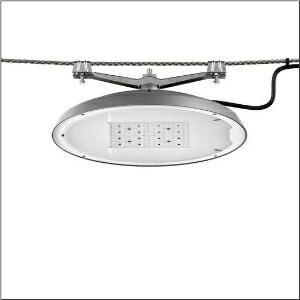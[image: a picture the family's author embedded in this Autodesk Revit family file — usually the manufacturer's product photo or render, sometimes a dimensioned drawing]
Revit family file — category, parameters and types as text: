
# Revit family: dl_50_iq_mini___st1_0s_5xa248w21f08le_fd6c
name_source: partatom
category: Lighting Fixtures
units: mm (PartAtom-declared; Revit-internal decimal feet)

## family parameters
Cut with Voids When Loaded = No
Host = Face
Light Source = No
Part Type = Normal
Room Calculation Point = No
Round Connector Dimension = Use Diameter
Shared = No

## types (1)
- --- (1 x LED, 8560 lm, 66.9 W, 2200K)
    Apparent Load = 67 VA
    CIE Flux Codes = 37 72 97 100 100
    Color Rendering = 70
    Color Temperature = 2200K
    Default Elevation = 1800 mm
    Description = DL 50 iQ mini, catenary luminaire, primary light control with lens, of PMMA, primary optical cover: cover, of toughened safety glass, transparent, light distribution: ST1.0s, light emission: direct distribution, primary light characteristic: symmetric, installation type: suspended mounting, LED, High Power LED, rated luminous flux: 8.560lm, luminous efficacy: 128lm/W, light colour: 722, colour temperature: 2200K, control gear: iQ Street-Remote, control: optimised constant luminous flux control (CLO 2.0), Desk-Remote (wireless, voltage-free reading and setting of iQ features in the workshop via application-optimized NFC function/RFID function), Light-Fading, Smart-Wire, Night-Set, Lumen-Switch, Temp-Guard, Auto-Match, Street-Remote, mains connection: 230..240V, AC, 50/60Hz, start of lifetime: 67W, end of service life: 70W, reduction: 31W, luminaire housing, of diecast aluminium, powder-coated, SITECO metallic grey (DB 702S), diameter: 500mm, height: 115mm, mounting height: 4..12m, protection rating (complete): IP66, insulation class (complete): insulation class II (safety insulation), certification: CE, ENEC, ENEC+, VDE, impact resistance: IK08, permissible operating ambient temperature for outdoor applications: -25..+40°C, standard-compliant lighting for roads and squares, packaging unit: 1 piece

Light Distribution: ST1.0s
    Height = 124 mm  [stored 0.406824 ft]
    Lamp = 1 x LED
    Lamp Light Flux = 8560 lm
    Lamp Power = 66.9 W
    Lamp count = 1
    Length = 500 mm
    Luminous efficacy = 128 lm/W
    Manufacturer = Siteco
    ModVariant = No
    Model = 5XA248W21F08LE
    Number of Poles = 1
    OnlyDefault = Yes
    Power Factor = 1
    Product Name = DL 50 iQ mini | ST1.0s
    Product group = catenary luminaire
    ProductGroupID = 6300
    Protection Class = Protection class II
    Protection Degree = IP 66
    RLX_Detail_Level = 1
    RLX_Emergency_Light_Flux = 0 lm
    RLX_Emergency_Type = 0
    RLX_Emergency_Type_DB = No
    RlxData = <blob elided: 127069 chars, md5=93f7c056>
    Socket = socket
    Standby Power = 0 W
    System Light Flux = 8560 lm
    System Power = 67 W
    Type Comments = factory setting: luminous flux: 100 % | dim-lin: 254 | 700 mA
    Type Image = l_1251783.jpg
    URL = http://relux.com
    VarID = @adj_140059
    Voltage = 0 V
    Weight = 0.00 kg
    Width = 0 mm  [stored 0 ft]

note: [stored X ft] marks values corroborated as IEEE doubles in the binary element streams (Revit-internal decimal feet)

## geometry (parser evidence)
native form markers: Blend x4, Sweep x14
no freeform markers — native parametric forms only
